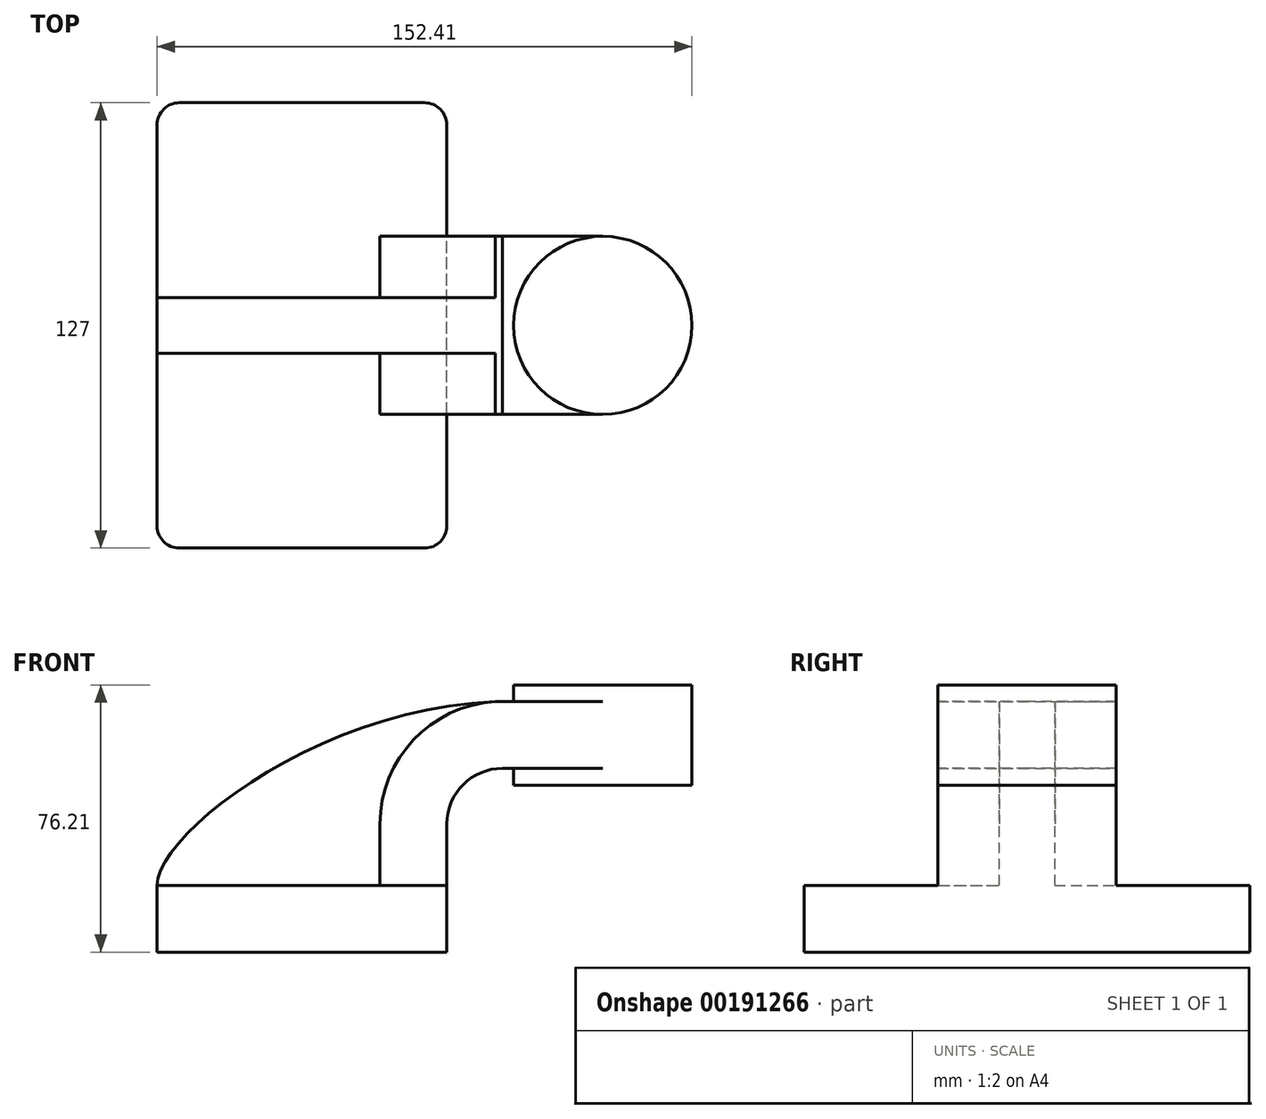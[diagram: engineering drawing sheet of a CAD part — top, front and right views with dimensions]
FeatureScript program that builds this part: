
annotation { "Feature Type Name" : "Feature", "Feature Type Description" : "" }
export const myFeature = defineFeature(function(context is Context, id is Id, definition is map)
    precondition{}
    {
        {
            var Q0;
            Q0=qCreatedBy(makeId("Front.planeOp"),FACE);
            var sketch = newSketch(context, id + "F0", { "sketchPlane" : qUnion([Q0])});
            skLineSegment(sketch, "E0.bottom", {"start": v(-41.28, 9.52) * mm, "end": v(41.27, 9.53) * mm});
            skLineSegment(sketch, "E0.top", {"start": v(-41.28, -9.52) * mm, "end": v(41.28, -9.52) * mm});
            skLineSegment(sketch, "E0.left", {"start": v(-41.28, 9.52) * mm, "end": v(-41.28, -9.53) * mm});
            skLineSegment(sketch, "E0.right", {"start": v(41.27, 9.53) * mm, "end": v(41.28, -9.52) * mm});
            skPoint(sketch, "E0.middle", {"position": v(0, 0) * mm});
            skPoint(sketch, "E1.middle", {"position": v(41.28, 74.79) * mm});
            skLineSegment(sketch, "E2", {"start": v(41.27, 9.53) * mm, "end": v(41.27, 27) * mm});
            skArc(sketch, "E3", {"start": v(41.27, 27) * mm, "mid": v(45.92, 38.23) * mm, "end": v(57.15, 42.88) * mm});
            skLineSegment(sketch, "E4.bottom", {"start": v(60.32, 66.68) * mm, "end": v(111.12, 66.68) * mm});
            skLineSegment(sketch, "E4.top", {"start": v(60.32, 38.1) * mm, "end": v(111.12, 38.1) * mm});
            skLineSegment(sketch, "E4.left", {"start": v(60.32, 66.67) * mm, "end": v(60.32, 38.1) * mm});
            skLineSegment(sketch, "E4.right", {"start": v(111.12, 66.67) * mm, "end": v(111.12, 38.1) * mm});
            skPoint(sketch, "E4.middle", {"position": v(85.72, 52.39) * mm});
            skLineSegment(sketch, "E5", {"start": v(57.15, 42.88) * mm, "end": v(85.72, 42.88) * mm});
            skLineSegment(sketch, "E6.0", {"start": v(57.15, 61.93) * mm, "end": v(85.72, 61.93) * mm});
            skArc(sketch, "E6.1", {"start": v(22.22, 27) * mm, "mid": v(32.45, 51.7) * mm, "end": v(57.15, 61.93) * mm});
            skLineSegment(sketch, "E6.2", {"start": v(22.22, 9.53) * mm, "end": v(22.22, 27) * mm});
            skLineSegment(sketch, "E7", {"start": v(85.72, 38.1) * mm, "end": v(85.72, 66.68) * mm});
            skFitSpline(sketch, "E8", {"points": [v(-41.28, 9.53) * mm, v(57.15, 61.93) * mm], "startDerivative": vector(0.24, 44.27) * mm, "endDerivative": vector(155.08, 3.13) * mm});
            skSolve(sketch);
        }
        {
            var Q0;
            Q0=makeQuery(id+"F0.imprint","IMPRINT",FACE,{"disambiguationData":[TD([[makeQuery(id+"F0.imprint","IMPRINT",EDGE,{"derivedFrom":sQuery(id+"F0.wireOp",EDGE,"E0.top")}),1.0]])]});
            extrude(context, id + "F1", {"entities" : qUnion([Q0]), "endBound" : BoundingType.SYMMETRIC, "depth" : 127 * mm});
        }
        {
            var Q0;
            {var subQ5=sQuery(id+"F0.wireOp",EDGE,"E2");Q0=makeQuery(id+"F0.imprint","IMPRINT",FACE,{"disambiguationData":[TD([[makeQuery(id+"F0.imprint","IMPRINT",EDGE,{"derivedFrom":subQ5}),1.0]])]});}
            var Q1;
            {var subQ0=sQuery(id+"F0.wireOp",EDGE,"E6.0");var subQ1=sQuery(id+"F0.wireOp",EDGE,"E4.left");var subQ2=makeQuery(id+"F0.imprint","INTERSECT",VERTEX,{"derivedFrom":[subQ1,subQ0]});Q1=makeQuery(id+"F0.imprint","IMPRINT",FACE,{"disambiguationData":[TD([[makeQuery(id+"F0.imprint","IMPRINT",EDGE,{"disambiguationData":[TD([[subQ2,-1.0]])],"derivedFrom":subQ1}),1.0]])]});}
            extrude(context, id + "F2", {"entities" : qUnion([Q0, Q1]), "operationType" : NewBodyOperationType.ADD, "endBound" : BoundingType.SYMMETRIC, "depth" : 50.8 * mm});
        }
        {
            var Q0;
            {var subQ3=sQuery(id+"F0.wireOp",EDGE,"E6.2");Q0=makeQuery(id+"F0.imprint","IMPRINT",FACE,{"disambiguationData":[TD([[makeQuery(id+"F0.imprint","IMPRINT",EDGE,{"derivedFrom":subQ3}),1.0]])]});}
            extrude(context, id + "F3", {"entities" : qUnion([Q0]), "operationType" : NewBodyOperationType.ADD, "endBound" : BoundingType.SYMMETRIC, "depth" : 15.88 * mm});
        }
        {
            var Q0;
            {var subQ4=sQuery(id+"F0.wireOp",EDGE,"E4.right");Q0=makeQuery(id+"F0.imprint","IMPRINT",FACE,{"disambiguationData":[TD([[makeQuery(id+"F0.imprint","IMPRINT",EDGE,{"derivedFrom":subQ4}),-1.0]])]});}
            var Q1;
            Q1=sQuery(id+"F0.wireOp",EDGE,"E7");
            revolve(context, id + "F4", {"operationType" : NewBodyOperationType.ADD, "entities" : qUnion([Q0]), "axis" : qUnion([Q1]), "revolveType" : RevolveType.FULL});
        }
        {
            var Q0;
            Q0=makeQuery(id+"F1.opExtrude","CAP_EDGE",EDGE,{"disambiguationData":[OSD([sQuery(id+"F0.wireOp",EDGE,"E0.right")])],"isStart":false});
            var Q1;
            Q1=makeQuery(id+"F1.opExtrude","CAP_EDGE",EDGE,{"disambiguationData":[OSD([sQuery(id+"F0.wireOp",EDGE,"E0.left")])],"isStart":false});
            var Q2;
            Q2=makeQuery(id+"F1.opExtrude","CAP_EDGE",EDGE,{"disambiguationData":[OSD([sQuery(id+"F0.wireOp",EDGE,"E0.right")])],"isStart":true});
            var Q3;
            Q3=makeQuery(id+"F1.opExtrude","CAP_EDGE",EDGE,{"disambiguationData":[OSD([sQuery(id+"F0.wireOp",EDGE,"E0.left")])],"isStart":true});
            fillet(context, id + "F5", {"entities" : qUnion([Q0, Q1, Q2, Q3]), "radius" : 6.35 * mm, "tangentPropagation" : true, "allowEdgeOverflow" : false});
        }
    });
